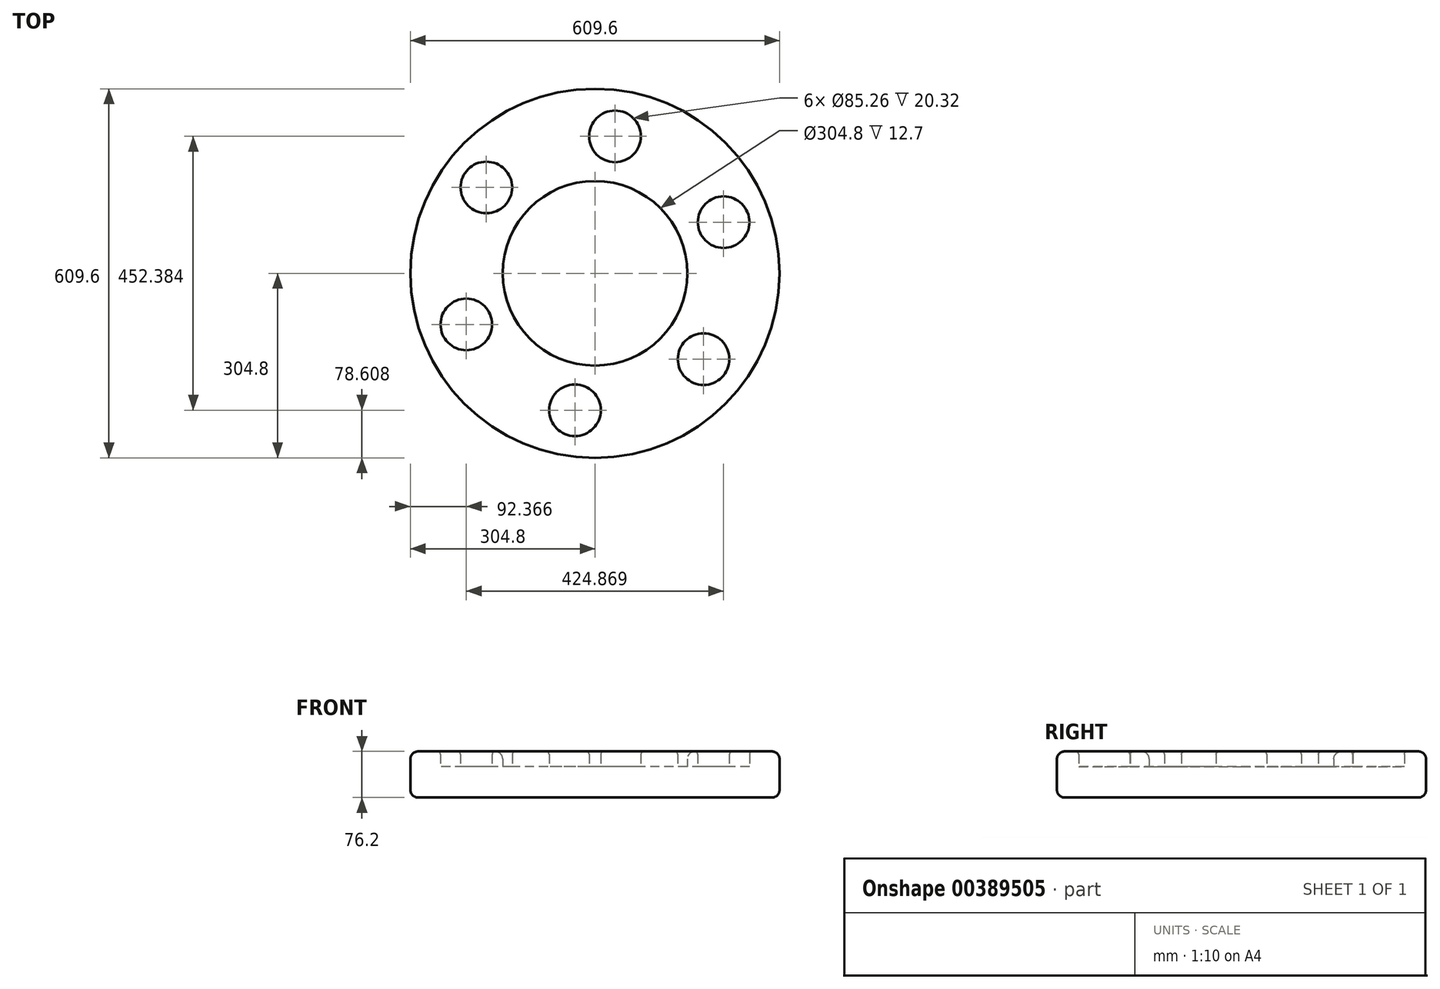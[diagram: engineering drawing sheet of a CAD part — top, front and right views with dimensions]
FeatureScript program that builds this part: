
annotation { "Feature Type Name" : "Feature", "Feature Type Description" : "" }
export const myFeature = defineFeature(function(context is Context, id is Id, definition is map)
    precondition{}
    {
        {
            var Q0;
            Q0=qCreatedBy(makeId("Top.planeOp"),FACE);
            var sketch = newSketch(context, id + "F0", { "sketchPlane" : qUnion([Q0])});
            skCircle(sketch, "E0", {"center": v(0, 0) * mm, "radius": 304.8 * mm});
            skCircle(sketch, "E1", {"center": v(0, 0) * mm, "radius": 152.4 * mm});
            skLineSegment(sketch, "E2", {"start": v(-239.12, 189) * mm, "end": v(-119.56, 94.5) * mm});
            skCircle(sketch, "E3", {"center": v(-179.34, 141.76) * mm, "radius": 42.63 * mm});
            skCircle(sketch, "E4.1.0", {"center": v(-212.43, -84.44) * mm, "radius": 42.63 * mm});
            skCircle(sketch, "E4.2.0", {"center": v(-33.1, -226.2) * mm, "radius": 42.63 * mm});
            skCircle(sketch, "E4.3.0", {"center": v(179.34, -141.76) * mm, "radius": 42.63 * mm});
            skCircle(sketch, "E4.4.0", {"center": v(212.43, 84.44) * mm, "radius": 42.63 * mm});
            skCircle(sketch, "E4.5.0", {"center": v(33.1, 226.2) * mm, "radius": 42.63 * mm});
            skSolve(sketch);
        }
        {
            var Q0;
            Q0=makeQuery(id+"F0.imprint","IMPRINT",FACE,{"disambiguationData":[TD([[makeQuery(id+"F0.imprint","IMPRINT",EDGE,{"derivedFrom":sQuery(id+"F0.wireOp",EDGE,"E1")}),1.0]])]});
            var Q1;
            Q1=makeQuery(id+"F0.imprint","IMPRINT",FACE,{"disambiguationData":[TD([[makeQuery(id+"F0.imprint","IMPRINT",EDGE,{"derivedFrom":sQuery(id+"F0.wireOp",EDGE,"E4.2.0")}),1.0]])]});
            var Q2;
            Q2=makeQuery(id+"F0.imprint","IMPRINT",FACE,{"disambiguationData":[TD([[makeQuery(id+"F0.imprint","IMPRINT",EDGE,{"derivedFrom":sQuery(id+"F0.wireOp",EDGE,"E4.3.0")}),1.0]])]});
            var Q3;
            Q3=makeQuery(id+"F0.imprint","IMPRINT",FACE,{"disambiguationData":[TD([[makeQuery(id+"F0.imprint","IMPRINT",EDGE,{"derivedFrom":sQuery(id+"F0.wireOp",EDGE,"E4.4.0")}),1.0]])]});
            var Q4;
            Q4=makeQuery(id+"F0.imprint","IMPRINT",FACE,{"disambiguationData":[TD([[makeQuery(id+"F0.imprint","IMPRINT",EDGE,{"derivedFrom":sQuery(id+"F0.wireOp",EDGE,"E4.5.0")}),1.0]])]});
            var Q5;
            {var subQ0=sQuery(id+"F0.wireOp",EDGE,"E3");var subQ1=sQuery(id+"F0.wireOp",EDGE,"E2");var subQ2=makeQuery(id+"F0.imprint","INTERSECT",VERTEX,{"disambiguationData":[OD(0.0)],"derivedFrom":[subQ1,subQ0]});Q5=makeQuery(id+"F0.imprint","IMPRINT",FACE,{"disambiguationData":[TD([[makeQuery(id+"F0.imprint","IMPRINT",EDGE,{"disambiguationData":[TD([[subQ2,-1.0]])],"derivedFrom":subQ1}),1.0]])]});}
            var Q6;
            {var subQ0=sQuery(id+"F0.wireOp",EDGE,"E3");var subQ1=sQuery(id+"F0.wireOp",EDGE,"E2");var subQ2=makeQuery(id+"F0.imprint","INTERSECT",VERTEX,{"disambiguationData":[OD(0.0)],"derivedFrom":[subQ1,subQ0]});Q6=makeQuery(id+"F0.imprint","IMPRINT",FACE,{"disambiguationData":[TD([[makeQuery(id+"F0.imprint","IMPRINT",EDGE,{"disambiguationData":[TD([[subQ2,-1.0]])],"derivedFrom":subQ1}),-1.0]])]});}
            var Q7;
            Q7=makeQuery(id+"F0.imprint","IMPRINT",FACE,{"disambiguationData":[TD([[makeQuery(id+"F0.imprint","IMPRINT",EDGE,{"derivedFrom":sQuery(id+"F0.wireOp",EDGE,"E4.1.0")}),1.0]])]});
            extrude(context, id + "F1", {"entities" : qUnion([Q0, Q1, Q2, Q3, Q4, Q5, Q6, Q7]), "depth" : 50.8 * mm});
        }
        {
            var Q0;
            Q0 = qSketchRegion(id + "F0", true);
            extrude(context, id + "F2", {"entities" : qUnion([Q0]), "operationType" : NewBodyOperationType.ADD, "depth" : 76.2 * mm});
        }
        {
            var Q0;
            Q0=makeQuery(id+"F2.opExtrude","CAP_EDGE",EDGE,{"disambiguationData":[OSD([sQuery(id+"F0.wireOp",EDGE,"E0")])],"isStart":false});
            var Q1;
            {var subQ0=sQuery(id+"F0.wireOp",EDGE,"E1");Q1=makeQuery(id+"F2.boolean.opBoolean","MERGE",FACE,{"derivedFrom":[makeQuery(id+"F1.opExtrude","CAP_FACE",FACE,{"disambiguationData":[OSD([subQ0])],"isStart":true}),makeQuery(id+"F2.opExtrude","CAP_FACE",FACE,{"disambiguationData":[OSD([sQuery(id+"F0.wireOp",EDGE,"E0"),subQ0,sQuery(id+"F0.wireOp",EDGE,"E3"),sQuery(id+"F0.wireOp",EDGE,"E4.1.0"),sQuery(id+"F0.wireOp",EDGE,"E4.2.0"),sQuery(id+"F0.wireOp",EDGE,"E4.3.0"),sQuery(id+"F0.wireOp",EDGE,"E4.4.0"),sQuery(id+"F0.wireOp",EDGE,"E4.5.0")])],"isStart":true})]});}
            var Q2;
            Q2=makeQuery(id+"F2.opExtrude","CAP_EDGE",EDGE,{"disambiguationData":[OSD([sQuery(id+"F0.wireOp",EDGE,"E1")])],"isStart":false});
            fillet(context, id + "F3", {"entities" : qUnion([Q0, Q1, Q2]), "radius" : 12.7 * mm, "tangentPropagation" : true, "allowEdgeOverflow" : false});
        }
        {
            var Q0;
            Q0=makeQuery(id+"F2.opExtrude","CAP_EDGE",EDGE,{"disambiguationData":[OSD([sQuery(id+"F0.wireOp",EDGE,"E4.1.0")])],"isStart":false});
            var Q1;
            Q1=makeQuery(id+"F2.opExtrude","CAP_EDGE",EDGE,{"disambiguationData":[OSD([sQuery(id+"F0.wireOp",EDGE,"E3")])],"isStart":false});
            var Q2;
            Q2=makeQuery(id+"F2.opExtrude","CAP_EDGE",EDGE,{"disambiguationData":[OSD([sQuery(id+"F0.wireOp",EDGE,"E4.5.0")])],"isStart":false});
            var Q3;
            Q3=makeQuery(id+"F2.opExtrude","CAP_EDGE",EDGE,{"disambiguationData":[OSD([sQuery(id+"F0.wireOp",EDGE,"E4.4.0")])],"isStart":false});
            var Q4;
            Q4=makeQuery(id+"F2.opExtrude","CAP_EDGE",EDGE,{"disambiguationData":[OSD([sQuery(id+"F0.wireOp",EDGE,"E4.2.0")])],"isStart":false});
            var Q5;
            Q5=makeQuery(id+"F2.opExtrude","CAP_EDGE",EDGE,{"disambiguationData":[OSD([sQuery(id+"F0.wireOp",EDGE,"E4.3.0")])],"isStart":false});
            fillet(context, id + "F4", {"entities" : qUnion([Q0, Q1, Q2, Q3, Q4, Q5]), "radius" : 5.08 * mm, "tangentPropagation" : true, "allowEdgeOverflow" : false});
        }
    });
